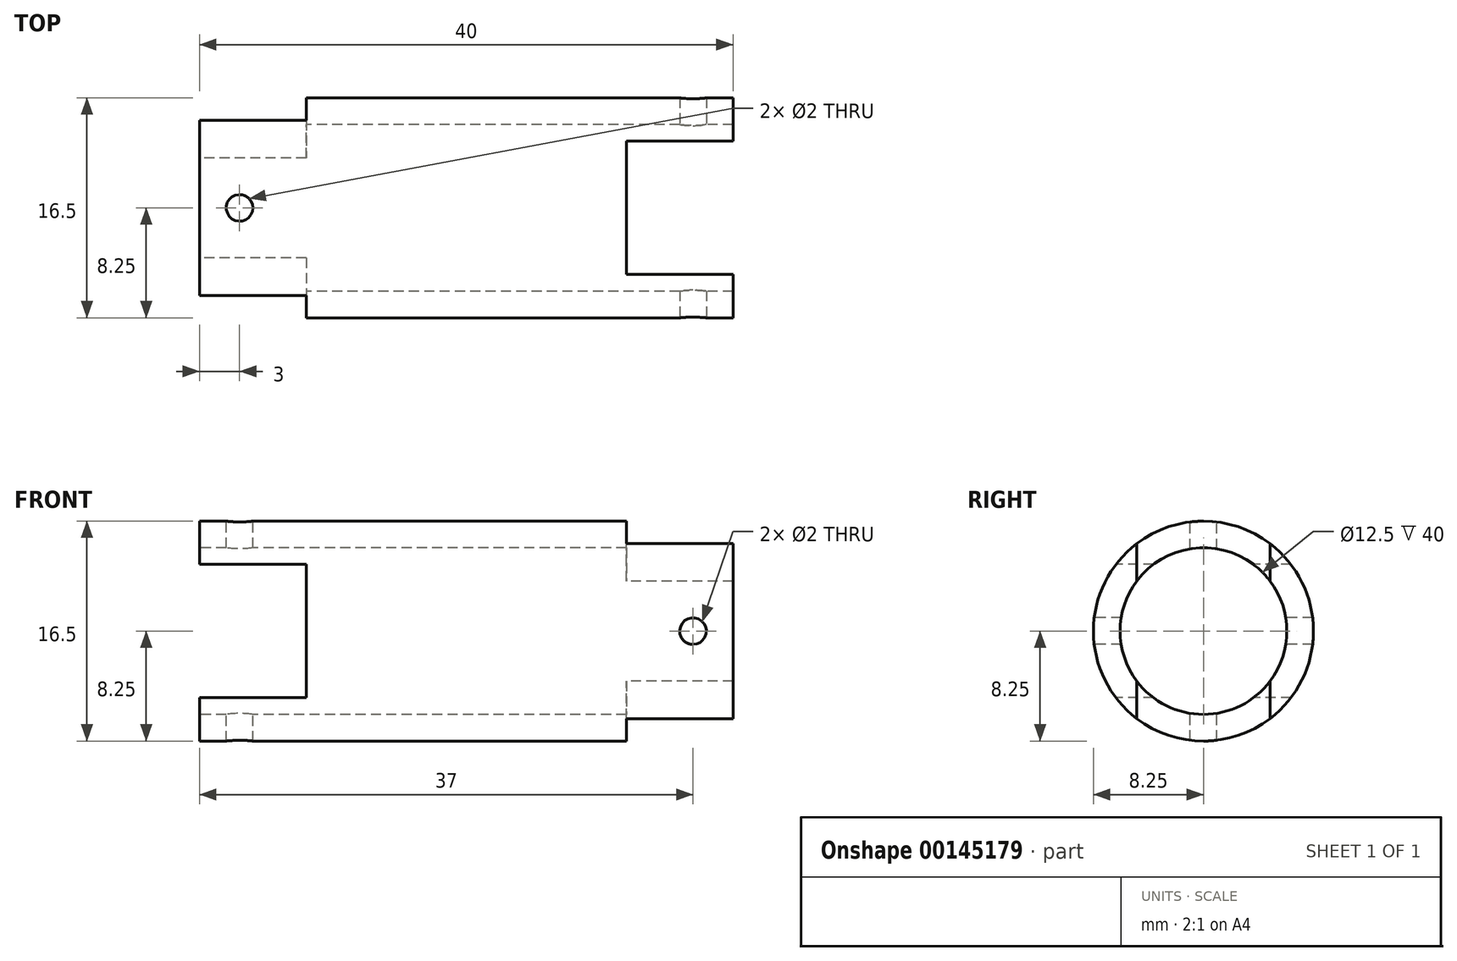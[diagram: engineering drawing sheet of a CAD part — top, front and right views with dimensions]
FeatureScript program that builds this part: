
annotation { "Feature Type Name" : "Feature", "Feature Type Description" : "" }
export const myFeature = defineFeature(function(context is Context, id is Id, definition is map)
    precondition{}
    {
        {
            var Q0;
            Q0=qCreatedBy(makeId("Right.planeOp"),FACE);
            var sketch = newSketch(context, id + "F0", { "sketchPlane" : qUnion([Q0])});
            skCircle(sketch, "E0", {"center": v(0, 0) * mm, "radius": 6.25 * mm});
            skCircle(sketch, "E1", {"center": v(0, 0) * mm, "radius": 8.25 * mm});
            skSolve(sketch);
        }
        {
            var Q0;
            Q0=makeQuery(id+"F0.imprint","IMPRINT",FACE,{"disambiguationData":[TD([[makeQuery(id+"F0.imprint","IMPRINT",EDGE,{"derivedFrom":sQuery(id+"F0.wireOp",EDGE,"E0")}),-1.0]])]});
            extrude(context, id + "F1", {"entities" : qUnion([Q0]), "depth" : 40 * mm});
        }
        {
            var Q0;
            Q0=qCreatedBy(makeId("Top.planeOp"),FACE);
            var sketch = newSketch(context, id + "F2", { "sketchPlane" : qUnion([Q0])});
            skLineSegment(sketch, "E2.bottom", {"start": v(52.54, -5) * mm, "end": v(32, -5) * mm});
            skLineSegment(sketch, "E2.top", {"start": v(52.54, 5) * mm, "end": v(32, 5) * mm});
            skLineSegment(sketch, "E2.left", {"start": v(52.54, -5) * mm, "end": v(52.54, 5) * mm});
            skLineSegment(sketch, "E2.right", {"start": v(32, -5) * mm, "end": v(32, 5) * mm});
            skCircle(sketch, "E3", {"center": v(3, 0) * mm, "radius": 1 * mm});
            skSolve(sketch);
        }
        {
            var Q0;
            Q0=makeQuery(id+"F2.imprint","IMPRINT",FACE,{"disambiguationData":[TD([[makeQuery(id+"F2.imprint","IMPRINT",EDGE,{"derivedFrom":sQuery(id+"F2.wireOp",EDGE,"E2.bottom")}),-1.0]])]});
            var Q1;
            Q1=makeQuery(id+"F2.imprint","IMPRINT",FACE,{"disambiguationData":[TD([[makeQuery(id+"F2.imprint","IMPRINT",EDGE,{"derivedFrom":sQuery(id+"F2.wireOp",EDGE,"E3")}),1.0]])]});
            extrude(context, id + "F3", {"entities" : qUnion([Q0, Q1]), "operationType" : NewBodyOperationType.REMOVE, "oppositeDirection" : true, "depth" : 25 * mm, "hasSecondDirection" : true, "secondDirectionOppositeDirection" : false, "secondDirectionDepth" : 25 * mm});
        }
        {
            var Q0;
            Q0=qCreatedBy(makeId("Front.planeOp"),FACE);
            var sketch = newSketch(context, id + "F4", { "sketchPlane" : qUnion([Q0])});
            skCircle(sketch, "E4", {"center": v(37, 0) * mm, "radius": 1 * mm});
            skLineSegment(sketch, "E5.bottom", {"start": v(8, -5) * mm, "end": v(-1.56, -5) * mm});
            skLineSegment(sketch, "E5.top", {"start": v(8, 5) * mm, "end": v(-1.56, 5) * mm});
            skLineSegment(sketch, "E5.left", {"start": v(8, -5) * mm, "end": v(8, 5) * mm});
            skLineSegment(sketch, "E5.right", {"start": v(-1.56, -5) * mm, "end": v(-1.56, 5) * mm});
            skSolve(sketch);
        }
        {
            var Q0;
            Q0=makeQuery(id+"F4.imprint","IMPRINT",FACE,{"disambiguationData":[TD([[makeQuery(id+"F4.imprint","IMPRINT",EDGE,{"derivedFrom":sQuery(id+"F4.wireOp",EDGE,"E4")}),1.0]])]});
            var Q1;
            Q1=makeQuery(id+"F4.imprint","IMPRINT",FACE,{"disambiguationData":[TD([[makeQuery(id+"F4.imprint","IMPRINT",EDGE,{"derivedFrom":sQuery(id+"F4.wireOp",EDGE,"E5.bottom")}),-1.0]])]});
            extrude(context, id + "F5", {"entities" : qUnion([Q0, Q1]), "operationType" : NewBodyOperationType.REMOVE, "oppositeDirection" : true, "depth" : 25 * mm, "hasSecondDirection" : true, "secondDirectionOppositeDirection" : false, "secondDirectionDepth" : 25 * mm});
        }
    });
